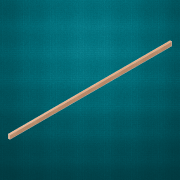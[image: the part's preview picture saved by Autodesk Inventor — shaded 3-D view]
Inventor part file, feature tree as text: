
AUTODESK INVENTOR PART (.ipt)
format: ipt  version: 2017 (Build 210142000, 142)  size: 116,224 bytes
history: native  units: in
note: dims shown in document units (in); Inventor stores cm internally (conversion verified against a paired STEP export)
features: extrude x1, sketch x1
ambient origin geometry x8: Origin, YZ Plane, XZ Plane, XY Plane, X Axis, Y Axis, Z Axis, Center Point
bodies: Solid1 (feature_tree)
feature tree (2):
  extrude  "Extrusion1"  Depth=1.875in
  sketch  "Sketch1"  dims[d0=0.875in d1=1.875in d2=78.375in d3=0.0in]
